# Revit family: monsun_r__ex_51fxc27a610a_30a8
name_source: partatom
category: Lighting Fixtures
units: mm (PartAtom-declared; Revit-internal decimal feet)

## family parameters
Cut with Voids When Loaded = No
Host = Face
Light Source = No
Part Type = Normal
Room Calculation Point = No
Round Connector Dimension = Use Diameter
Shared = No

## types (1)
- Monsun® Ex (1 x LED, 1600 lm, 13 W, 6500K)
    Apparent Load = 13 VA
    CIE Flux Codes = 40 70 89 90 100
    Color Rendering = 80
    Color Temperature = 6500K
    Default Elevation = 1800 mm
    Description = Monsun® Ex, damp-proof luminaire, primary optical cover: cover, of PC, UV-stabilised, opal, light emission: direct distribution, primary light characteristic: symmetric, installation type: surface-mounted, LED, rated luminous flux: 1.600lm, luminous efficacy: 123lm/W, light colour: 865, colour temperature: 6500K, control gear: ON/OFF, with terminal, 3-pole, max. 2.5mm², through-wiring: 5x 2.5mm², mains connection: 220..240V, AC, 50/60Hz, rated input power: 13W, housing, of PC, light grey (RAL 7035), incl. 2x Ex cable gland M20 for cable diameter 7..12mm with sealing, incl. 3x Ex locking screw M20 with sealing, length: 338mm, width: 176mm, height: 110mm, clip for enclosure, of stainless steel, protection rating (complete): IP66, insulation class (complete): insulation class I (protective earthing), certification: CE, explosion class: zone 2,22 II 3G Ex nR IIC T6 GC, II3D Ex tc IIIC T65°C Dc, impact resistance: IK10, permissible operating ambient temperature: -20..+50°C, LABS conformity tested according to VDMA 24364:2018-05, contact your sales advisor before using the luminaires in applications with unclear chemical exposure, large temperature fluctuations or condensation-forming humidity, packaging unit: 1 piece
    Height = 110 mm
    Lamp = 1 x LED
    Lamp Light Flux = 1600 lm
    Lamp Power = 13 W
    Lamp count = 1
    Length = 338 mm
    Luminous efficacy = 123 lm/W
    Manufacturer = Siteco
    ModVariant = No
    Model = 51FXC27A610A
    Mounting Place = Ceiling
    Mounting Type = Surface mounted
    Number of Poles = 1
    OnlyDefault = Yes
    Power Factor = 1
    Product Name = Monsun® Ex
    Product group = damp-proof luminaire
    ProductGroupID = 301
    Protection Class = Protection class I
    Protection Degree = IP 66
    RLX_Detail_Level = 1
    RLX_Emergency_Light_Flux = 0 lm
    RLX_Emergency_Type = 0
    RLX_Emergency_Type_DB = No
    RlxData = <blob elided: 50693 chars, md5=ac6d4f14>
    Socket = socket
    Standby Power = 0 W
    System Light Flux = 1600 lm
    System Power = 13 W
    Type Comments = Product without accessories
    Type Image = l_1258884.jpg
    URL = http://relux.com
    VarID = ---
    Voltage = 0 V
    Weight = 0.00 kg
    Width = 176 mm

## geometry (parser evidence)
native form markers: Sweep x12
no freeform markers — native parametric forms only
